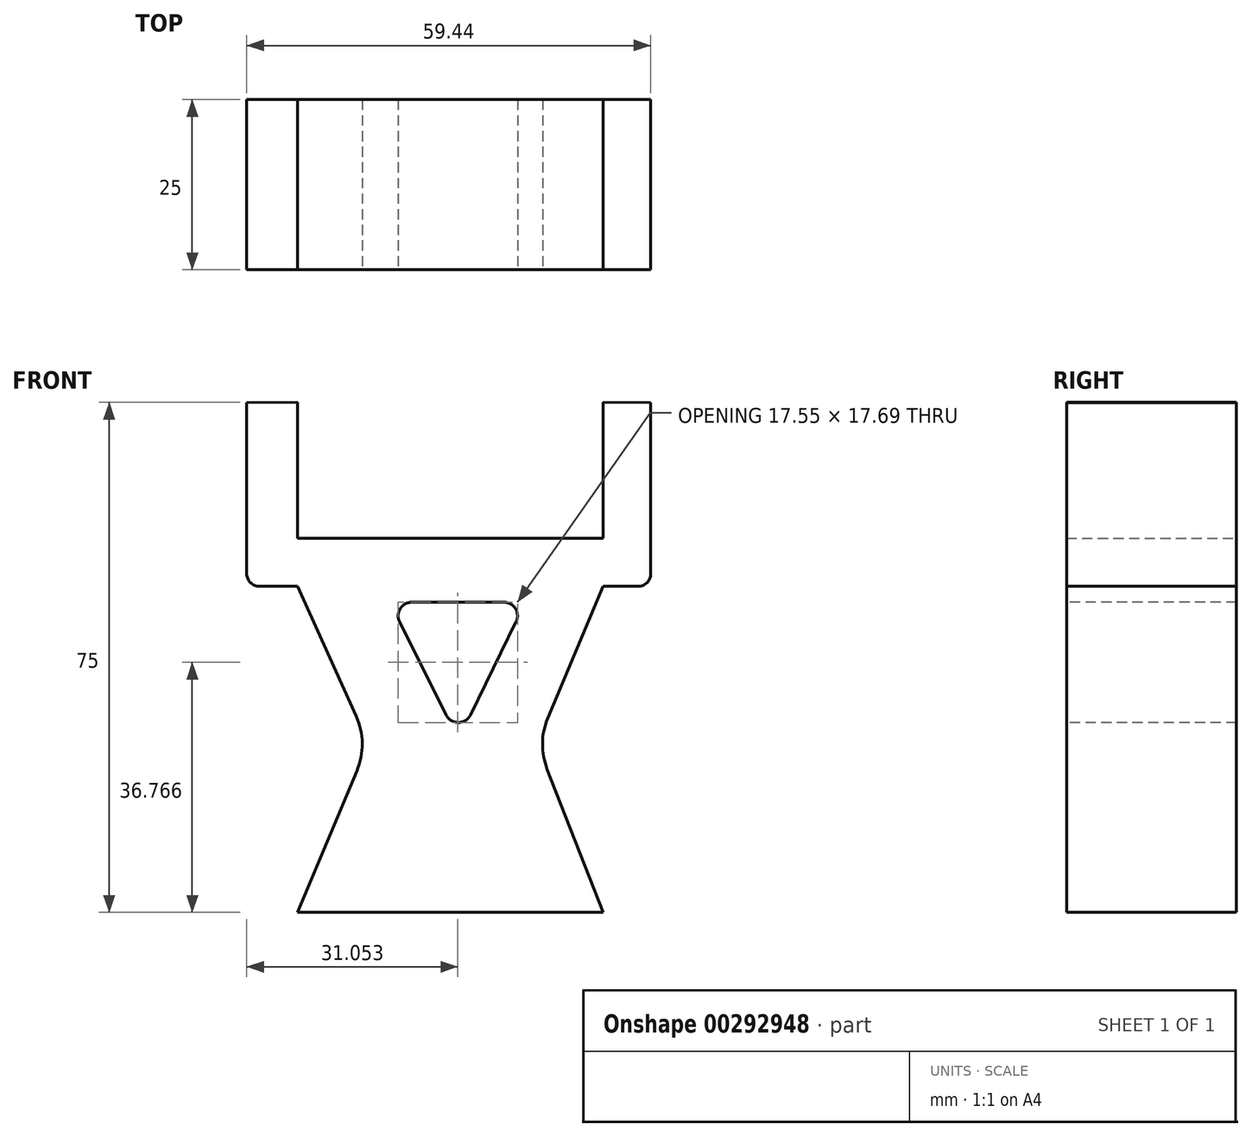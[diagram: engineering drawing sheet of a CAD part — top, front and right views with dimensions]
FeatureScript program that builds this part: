
annotation { "Feature Type Name" : "Feature", "Feature Type Description" : "" }
export const myFeature = defineFeature(function(context is Context, id is Id, definition is map)
    precondition{}
    {
        {
            var Q0;
            Q0=qCreatedBy(makeId("Front.planeOp"),FACE);
            var sketch = newSketch(context, id + "F0", { "sketchPlane" : qUnion([Q0])});
            skLineSegment(sketch, "E0.bottom", {"start": v(-45, -71.78) * mm, "end": v(0, -71.78) * mm});
            skLineSegment(sketch, "E0.top", {"start": v(-45, -126.78) * mm, "end": v(0, -126.78) * mm});
            skLineSegment(sketch, "E0.left", {"start": v(-45, -71.78) * mm, "end": v(-45, -126.78) * mm});
            skLineSegment(sketch, "E0.right", {"start": v(0, -71.78) * mm, "end": v(0, -126.78) * mm});
            skSolve(sketch);
        }
        {
            var Q0;
            Q0=makeQuery(id+"F0.imprint","IMPRINT",FACE,{"disambiguationData":[TD([[makeQuery(id+"F0.imprint","IMPRINT",EDGE,{"derivedFrom":sQuery(id+"F0.wireOp",EDGE,"E0.bottom")}),-1.0]])]});
            extrude(context, id + "F1", {"entities" : qUnion([Q0]), "depth" : 25 * mm});
        }
        {
            var Q0;
            Q0=makeQuery(id+"F1.opExtrude","CAP_FACE",FACE,{"disambiguationData":[OSD([sQuery(id+"F0.wireOp",EDGE,"E0.bottom"),sQuery(id+"F0.wireOp",EDGE,"E0.top"),sQuery(id+"F0.wireOp",EDGE,"E0.left"),sQuery(id+"F0.wireOp",EDGE,"E0.right")])],"isStart":false});
            var sketch = newSketch(context, id + "F2", { "sketchPlane" : qUnion([Q0])});
            skLineSegment(sketch, "E1", {"start": v(0, -71.78) * mm, "end": v(0, -51.78) * mm});
            skLineSegment(sketch, "E2", {"start": v(0, -78.83) * mm, "end": v(5.14, -78.83) * mm});
            skLineSegment(sketch, "E3", {"start": v(7, -76.96) * mm, "end": v(7, -51.83) * mm});
            skLineSegment(sketch, "E4", {"start": v(-45, -78.83) * mm, "end": v(-50.58, -78.83) * mm});
            skLineSegment(sketch, "E5", {"start": v(-52.44, -76.96) * mm, "end": v(-52.44, -51.83) * mm});
            skLineSegment(sketch, "E6", {"start": v(-45, -71.78) * mm, "end": v(-45, -51.78) * mm});
            skLineSegment(sketch, "E7", {"start": v(0, -71.78) * mm, "end": v(0, -78.83) * mm});
            skLineSegment(sketch, "E8", {"start": v(0, -51.78) * mm, "end": v(7, -51.83) * mm});
            skLineSegment(sketch, "E9", {"start": v(-52.44, -51.83) * mm, "end": v(-45, -51.78) * mm});
            skPoint(sketch, "E10.visualSharp", {"position": v(7, -78.83) * mm});
            skArc(sketch, "E10.filletArc", {"start": v(5.14, -78.83) * mm, "mid": v(6.45, -78.28) * mm, "end": v(7, -76.96) * mm});
            skPoint(sketch, "E11.visualSharp", {"position": v(-52.44, -78.83) * mm});
            skArc(sketch, "E11.filletArc", {"start": v(-52.44, -76.96) * mm, "mid": v(-51.9, -78.28) * mm, "end": v(-50.58, -78.83) * mm});
            skSolve(sketch);
        }
        {
            var Q0;
            Q0=makeQuery(id+"F2.imprint","IMPRINT",FACE,{"disambiguationData":[TD([[makeQuery(id+"F2.imprint","IMPRINT",EDGE,{"derivedFrom":sQuery(id+"F2.wireOp",EDGE,"E1")}),-1.0]])]});
            var Q1;
            {var subQ1=sQuery(id+"F2.wireOp",EDGE,"E4");Q1=makeQuery(id+"F2.imprint","IMPRINT",FACE,{"disambiguationData":[TD([[makeQuery(id+"F2.imprint","IMPRINT",EDGE,{"derivedFrom":subQ1}),-1.0]])]});}
            extrude(context, id + "F3", {"entities" : qUnion([Q0, Q1]), "operationType" : NewBodyOperationType.ADD, "oppositeDirection" : true, "depth" : 25 * mm});
        }
        {
            var Q0;
            {var subQ0=sQuery(id+"F0.wireOp",EDGE,"E0.left");Q0=makeQuery(id+"F3.boolean.opBoolean","MERGE",FACE,{"derivedFrom":[makeQuery(id+"F1.opExtrude","CAP_FACE",FACE,{"disambiguationData":[OSD([sQuery(id+"F0.wireOp",EDGE,"E0.bottom"),sQuery(id+"F0.wireOp",EDGE,"E0.top"),subQ0,sQuery(id+"F0.wireOp",EDGE,"E0.right")])],"isStart":false}),makeQuery(id+"F3.opExtrude","CAP_FACE",FACE,{"disambiguationData":[OSD([sQuery(id+"F2.wireOp",EDGE,"E1"),sQuery(id+"F2.wireOp",EDGE,"E2"),sQuery(id+"F2.wireOp",EDGE,"E3"),sQuery(id+"F2.wireOp",EDGE,"E7"),sQuery(id+"F2.wireOp",EDGE,"E8")])],"isStart":true}),makeQuery(id+"F3.opExtrude","CAP_FACE",FACE,{"disambiguationData":[OSD([subQ0,sQuery(id+"F2.wireOp",EDGE,"E4"),sQuery(id+"F2.wireOp",EDGE,"E5"),sQuery(id+"F2.wireOp",EDGE,"E6"),sQuery(id+"F2.wireOp",EDGE,"E9")])],"isStart":true})]});}
            var sketch = newSketch(context, id + "F4", { "sketchPlane" : qUnion([Q0])});
            skLineSegment(sketch, "E12", {"start": v(-45, -78.83) * mm, "end": v(-36.34, -97.95) * mm});
            skLineSegment(sketch, "E13", {"start": v(-36.24, -105.95) * mm, "end": v(-45, -126.78) * mm});
            skLineSegment(sketch, "E14", {"start": v(0, -78.83) * mm, "end": v(-8.15, -98.19) * mm});
            skLineSegment(sketch, "E15", {"start": v(-8.24, -105.71) * mm, "end": v(0, -126.78) * mm});
            skPoint(sketch, "E16.visualSharp", {"position": v(-9.72, -101.93) * mm});
            skArc(sketch, "E16.filletArc", {"start": v(-8.15, -98.19) * mm, "mid": v(-8.93, -101.94) * mm, "end": v(-8.24, -105.71) * mm});
            skPoint(sketch, "E17.visualSharp", {"position": v(-34.54, -101.93) * mm});
            skArc(sketch, "E17.filletArc", {"start": v(-36.24, -105.95) * mm, "mid": v(-35.46, -101.94) * mm, "end": v(-36.34, -97.95) * mm});
            skSolve(sketch);
        }
        {
            var Q0;
            Q0 = qSketchRegion(id + "F4", true);
            var Q1;
            Q1=makeQuery(id+"F4.imprint","IMPRINT",FACE,{"disambiguationData":[TD([[makeQuery(id+"F4.imprint","IMPRINT",EDGE,{"derivedFrom":sQuery(id+"F4.wireOp",EDGE,"E14")}),1.0]])]});
            var Q2;
            Q2=makeQuery(id+"F4.imprint","IMPRINT",FACE,{"disambiguationData":[TD([[makeQuery(id+"F4.imprint","IMPRINT",EDGE,{"derivedFrom":sQuery(id+"F4.wireOp",EDGE,"E12")}),-1.0]])]});
            extrude(context, id + "F5", {"entities" : qUnion([Q0, Q1, Q2]), "operationType" : NewBodyOperationType.REMOVE, "oppositeDirection" : true, "depth" : 25 * mm});
        }
        {
            var Q0;
            {var subQ0=sQuery(id+"F0.wireOp",EDGE,"E0.left");Q0=makeQuery(id+"F3.boolean.opBoolean","MERGE",FACE,{"derivedFrom":[makeQuery(id+"F1.opExtrude","CAP_FACE",FACE,{"disambiguationData":[OSD([sQuery(id+"F0.wireOp",EDGE,"E0.bottom"),sQuery(id+"F0.wireOp",EDGE,"E0.top"),subQ0,sQuery(id+"F0.wireOp",EDGE,"E0.right")])],"isStart":false}),makeQuery(id+"F3.opExtrude","CAP_FACE",FACE,{"disambiguationData":[OSD([sQuery(id+"F2.wireOp",EDGE,"E1"),sQuery(id+"F2.wireOp",EDGE,"E2"),sQuery(id+"F2.wireOp",EDGE,"E3"),sQuery(id+"F2.wireOp",EDGE,"E7"),sQuery(id+"F2.wireOp",EDGE,"E8"),sQuery(id+"F2.wireOp",EDGE,"E10.filletArc")])],"isStart":true}),makeQuery(id+"F3.opExtrude","CAP_FACE",FACE,{"disambiguationData":[OSD([subQ0,sQuery(id+"F2.wireOp",EDGE,"E4"),sQuery(id+"F2.wireOp",EDGE,"E5"),sQuery(id+"F2.wireOp",EDGE,"E6"),sQuery(id+"F2.wireOp",EDGE,"E9"),sQuery(id+"F2.wireOp",EDGE,"E11.filletArc")])],"isStart":true})]});}
            var sketch = newSketch(context, id + "F6", { "sketchPlane" : qUnion([Q0])});
            skLineSegment(sketch, "E18", {"start": v(-14.6, -81.17) * mm, "end": v(-28.17, -81.17) * mm});
            skLineSegment(sketch, "E19", {"start": v(-14.6, -81.17) * mm, "end": v(-21.4, -81.17) * mm});
            skLineSegment(sketch, "E20", {"start": v(-12.81, -84.05) * mm, "end": v(-19.52, -97.74) * mm});
            skLineSegment(sketch, "E21", {"start": v(-29.95, -84.06) * mm, "end": v(-23.1, -97.75) * mm});
            skPoint(sketch, "E22.visualSharp", {"position": v(-31.4, -81.17) * mm});
            skArc(sketch, "E22.filletArc", {"start": v(-28.17, -81.17) * mm, "mid": v(-29.87, -82.12) * mm, "end": v(-29.95, -84.06) * mm});
            skPoint(sketch, "E23.visualSharp", {"position": v(-11.4, -81.17) * mm});
            skArc(sketch, "E23.filletArc", {"start": v(-12.81, -84.05) * mm, "mid": v(-12.91, -82.11) * mm, "end": v(-14.6, -81.17) * mm});
            skPoint(sketch, "E24.visualSharp", {"position": v(-21.3, -101.37) * mm});
            skArc(sketch, "E24.filletArc", {"start": v(-23.1, -97.75) * mm, "mid": v(-21.31, -98.86) * mm, "end": v(-19.52, -97.74) * mm});
            skSolve(sketch);
        }
        {
            var Q0;
            Q0 = qSketchRegion(id + "F6", true);
            extrude(context, id + "F7", {"entities" : qUnion([Q0]), "operationType" : NewBodyOperationType.REMOVE, "oppositeDirection" : true, "depth" : 42.3 * mm});
        }
    });
